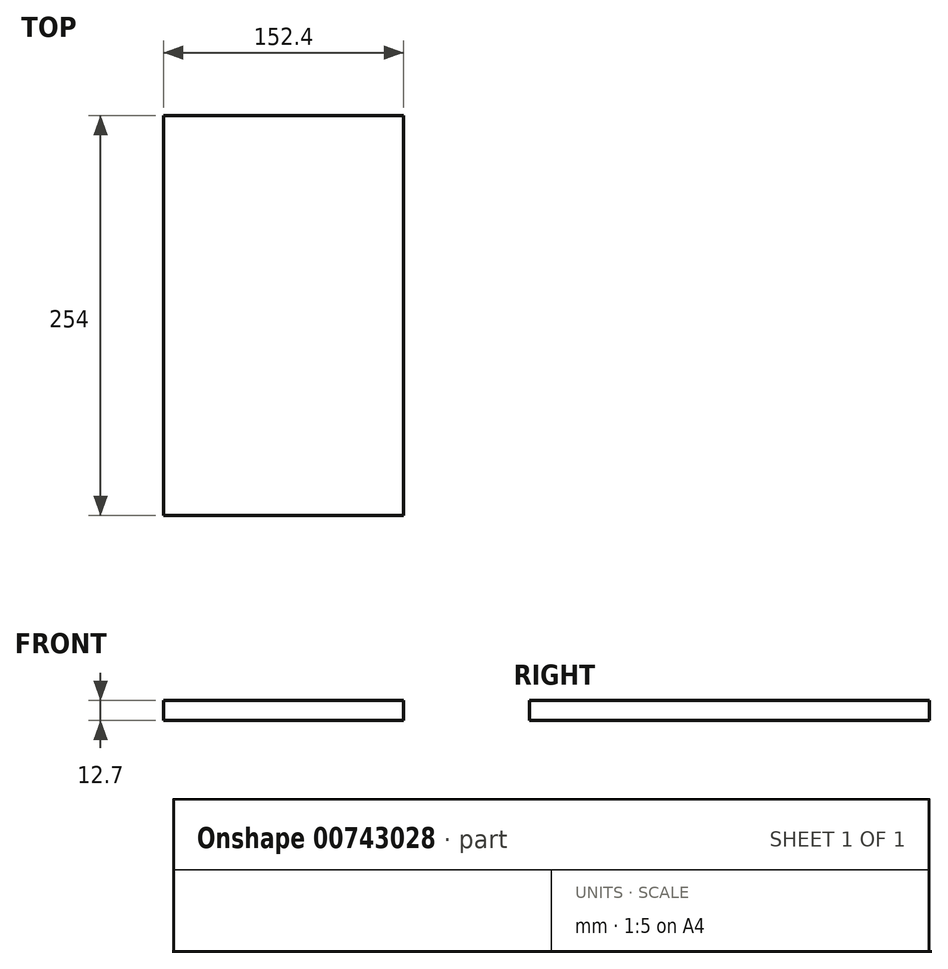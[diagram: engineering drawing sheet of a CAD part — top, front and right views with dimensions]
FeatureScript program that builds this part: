
annotation { "Feature Type Name" : "Feature", "Feature Type Description" : "" }
export const myFeature = defineFeature(function(context is Context, id is Id, definition is map)
    precondition{}
    {
        {
            var Q0;
            Q0=qCreatedBy(makeId("Top.planeOp"),FACE);
            var sketch = newSketch(context, id + "F0", { "sketchPlane" : qUnion([Q0])});
            skLineSegment(sketch, "E0.bottom", {"start": v(-76.2, -127) * mm, "end": v(76.2, -127) * mm});
            skLineSegment(sketch, "E0.top", {"start": v(-76.2, 127) * mm, "end": v(76.2, 127) * mm});
            skLineSegment(sketch, "E0.left", {"start": v(-76.2, -127) * mm, "end": v(-76.2, 127) * mm});
            skLineSegment(sketch, "E0.right", {"start": v(76.2, -127) * mm, "end": v(76.2, 127) * mm});
            skPoint(sketch, "E0.middle", {"position": v(0, 0) * mm});
            skSolve(sketch);
        }
        {
            var Q0;
            Q0 = qSketchRegion(id + "F0", true);
            extrude(context, id + "F1", {"entities" : qUnion([Q0]), "oppositeDirection" : true, "depth" : 12.7 * mm, "offsetDistance" : 25.4 * mm});
        }
    });
